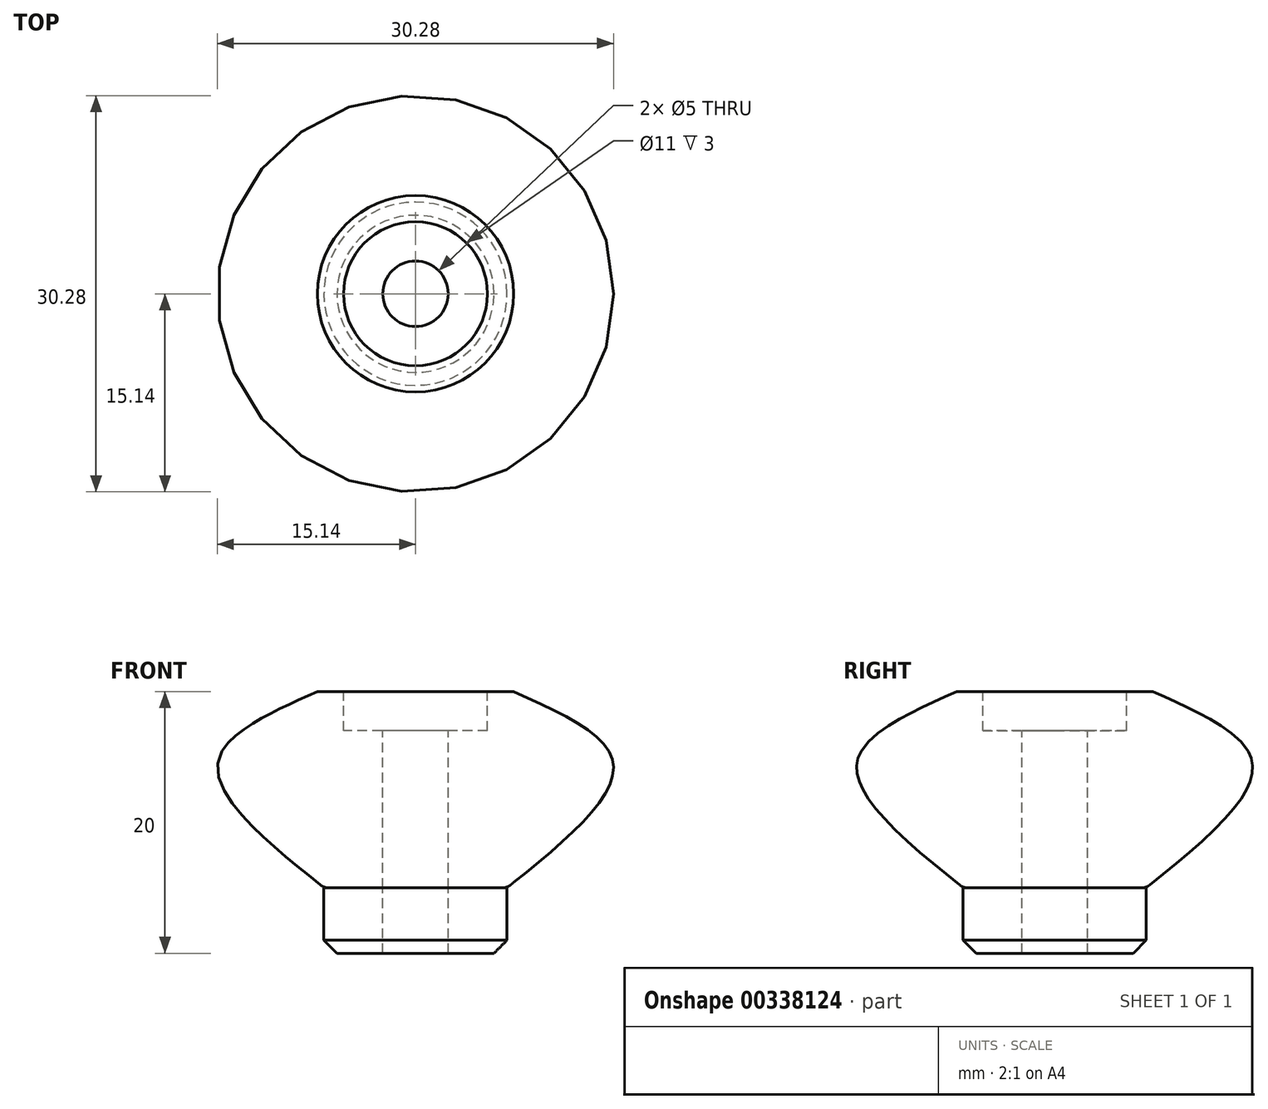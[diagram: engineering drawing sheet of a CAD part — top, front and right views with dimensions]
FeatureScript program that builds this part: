
annotation { "Feature Type Name" : "Feature", "Feature Type Description" : "" }
export const myFeature = defineFeature(function(context is Context, id is Id, definition is map)
    precondition{}
    {
        {
            var Q0;
            Q0=qCreatedBy(makeId("Top.planeOp"),FACE);
            var sketch = newSketch(context, id + "F0", { "sketchPlane" : qUnion([Q0])});
            skCircle(sketch, "E0", {"center": v(0, 0) * mm, "radius": 7 * mm});
            skSolve(sketch);
        }
        {
            var Q0;
            Q0 = qSketchRegion(id + "F0", true);
            extrude(context, id + "F1", {"entities" : qUnion([Q0]), "depth" : 5 * mm});
        }
        {
            var Q0;
            Q0=qCreatedBy(makeId("Top.planeOp"),FACE);
            cPlane(context, id + "F2", {"entities" : qUnion([Q0]), "cplaneType" : CPlaneType.OFFSET, "offset" : 20 * mm, "width" : 150 * mm, "height" : 150 * mm});
        }
        {
            var Q0;
            Q0=qCreatedBy(makeId("Top.planeOp"),FACE);
            cPlane(context, id + "F3", {"entities" : qUnion([Q0]), "cplaneType" : CPlaneType.OFFSET, "offset" : 15 * mm, "width" : 150 * mm, "height" : 150 * mm});
        }
        {
            var Q0;
            Q0=qCreatedBy(id+"F2.planeOp",FACE);
            var sketch = newSketch(context, id + "F4", { "sketchPlane" : qUnion([Q0])});
            skCircle(sketch, "E1", {"center": v(0, 0) * mm, "radius": 7.5 * mm});
            skSolve(sketch);
        }
        {
            var Q0;
            Q0=qCreatedBy(id+"F3.planeOp",FACE);
            var sketch = newSketch(context, id + "F5", { "sketchPlane" : qUnion([Q0])});
            skCircle(sketch, "E2", {"center": v(0, 0) * mm, "radius": 15 * mm});
            skSolve(sketch);
        }
        {
            var Q0;
            Q0=makeQuery(id+"F4.imprint","IMPRINT",FACE,{"disambiguationData":[TD([[makeQuery(id+"F4.imprint","IMPRINT",EDGE,{"derivedFrom":sQuery(id+"F4.wireOp",EDGE,"E1")}),1.0]])]});
            var Q1;
            Q1=makeQuery(id+"F5.imprint","IMPRINT",FACE,{"disambiguationData":[TD([[makeQuery(id+"F5.imprint","IMPRINT",EDGE,{"derivedFrom":sQuery(id+"F5.wireOp",EDGE,"E2")}),1.0]])]});
            var Q2;
            Q2=makeQuery(id+"F1.opExtrude","CAP_FACE",FACE,{"disambiguationData":[OSD([sQuery(id+"F0.wireOp",EDGE,"E0")])],"isStart":false});
            loft(context, id + "F6", {"sheetProfilesArray" : [{ "sheetProfileEntities" : qUnion([Q0]) }, { "sheetProfileEntities" : qUnion([Q1]) }, { "sheetProfileEntities" : qUnion([Q2]) }]});
        }
        {
            var Q0;
            Q0=makeQuery(id+"F4.imprint","IMPRINT",FACE,{"disambiguationData":[TD([[makeQuery(id+"F4.imprint","IMPRINT",EDGE,{"derivedFrom":sQuery(id+"F4.wireOp",EDGE,"E1")}),1.0]])]});
            var sketch = newSketch(context, id + "F7", { "sketchPlane" : qUnion([Q0])});
            skCircle(sketch, "E3", {"center": v(0, 0) * mm, "radius": 2.5 * mm});
            skSolve(sketch);
        }
        {
            var Q0;
            Q0 = qSketchRegion(id + "F7", true);
            extrude(context, id + "F8", {"entities" : qUnion([Q0]), "operationType" : NewBodyOperationType.REMOVE, "endBound" : BoundingType.THROUGH_ALL, "oppositeDirection" : true, "depth" : 25 * mm});
        }
        {
            var Q0;
            Q0=makeQuery(id+"F4.imprint","IMPRINT",FACE,{"disambiguationData":[TD([[makeQuery(id+"F4.imprint","IMPRINT",EDGE,{"derivedFrom":sQuery(id+"F4.wireOp",EDGE,"E1")}),1.0]])]});
            var sketch = newSketch(context, id + "F9", { "sketchPlane" : qUnion([Q0])});
            skCircle(sketch, "E4", {"center": v(0, 0) * mm, "radius": 5.5 * mm});
            skSolve(sketch);
        }
        {
            var Q0;
            Q0 = qSketchRegion(id + "F9", true);
            extrude(context, id + "F10", {"entities" : qUnion([Q0]), "operationType" : NewBodyOperationType.REMOVE, "oppositeDirection" : true, "depth" : 3 * mm});
        }
        {
            var Q0;
            Q0=makeQuery(id+"F6.opLoft","MID_CAP_EDGE",EDGE,{"disambiguationData":[OSD([sQuery(id+"F0.wireOp",EDGE,"E0"),sQuery(id+"F4.wireOp",EDGE,"E1")])],"capPos":2.0});
            fillet(context, id + "F11", {"entities" : qUnion([Q0]), "radius" : 1 * mm, "tangentPropagation" : true, "allowEdgeOverflow" : false});
        }
        {
            var Q0;
            Q0=makeQuery(id+"F1.opExtrude","CAP_EDGE",EDGE,{"disambiguationData":[OSD([sQuery(id+"F0.wireOp",EDGE,"E0")])],"isStart":true});
            chamfer(context, id + "F12", {"entities" : qUnion([Q0]), "chamferType" : ChamferType.OFFSET_ANGLE, "width" : 1 * mm, "oppositeDirection" : false, "angle" : 45 * degree, "tangentPropagation" : true});
        }
    });
